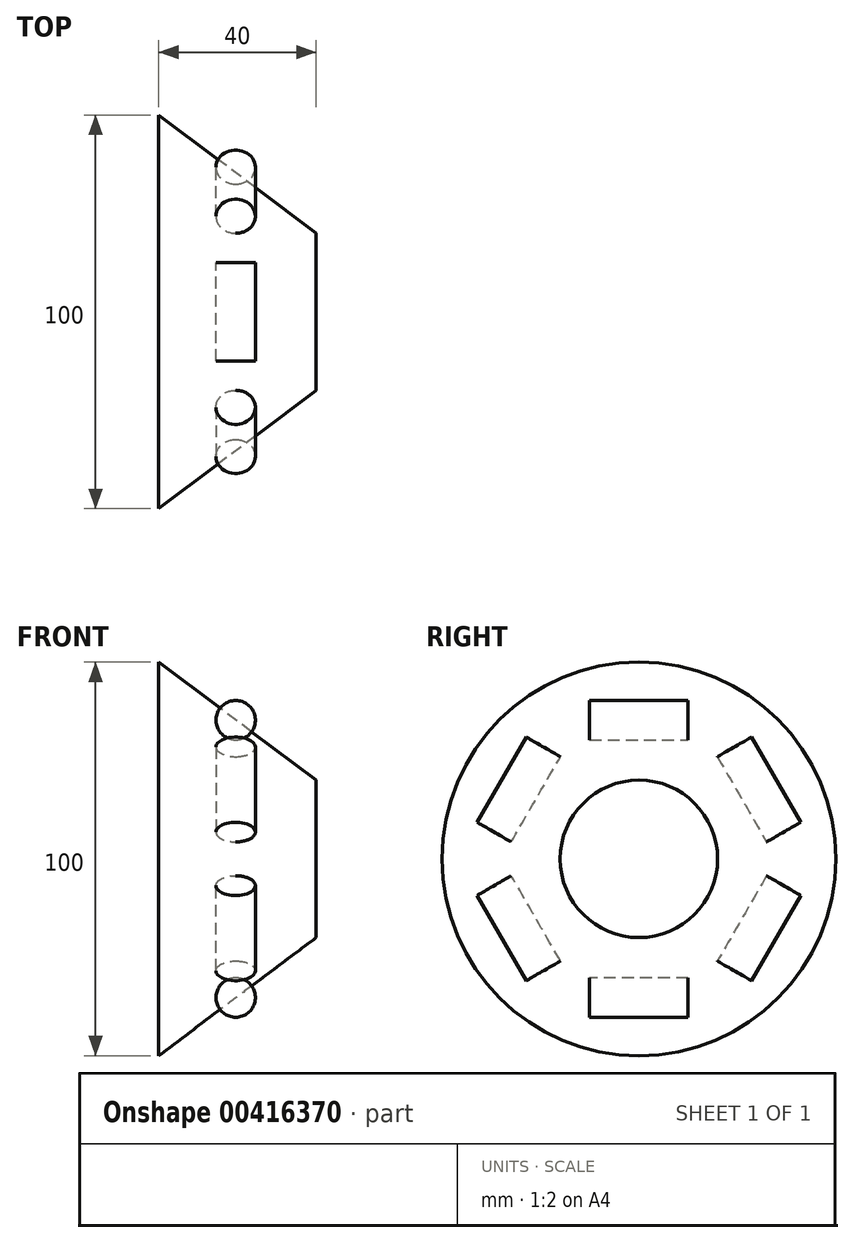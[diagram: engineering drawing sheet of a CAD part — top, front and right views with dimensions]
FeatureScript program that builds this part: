
annotation { "Feature Type Name" : "Feature", "Feature Type Description" : "" }
export const myFeature = defineFeature(function(context is Context, id is Id, definition is map)
    precondition{}
    {
        {
            var Q0;
            Q0=qCreatedBy(makeId("Right.planeOp"),FACE);
            var sketch = newSketch(context, id + "F0", { "sketchPlane" : qUnion([Q0])});
            skCircle(sketch, "E0", {"center": v(0, 0) * mm, "radius": 50 * mm});
            skSolve(sketch);
        }
        {
            var Q0;
            Q0=qCreatedBy(makeId("Right.planeOp"),FACE);
            cPlane(context, id + "F1", {"entities" : qUnion([Q0]), "cplaneType" : CPlaneType.OFFSET, "offset" : 40 * mm, "width" : 150 * mm, "height" : 150 * mm});
        }
        {
            var Q0;
            Q0=qCreatedBy(id+"F1.planeOp",FACE);
            var sketch = newSketch(context, id + "F2", { "sketchPlane" : qUnion([Q0])});
            skCircle(sketch, "E1", {"center": v(0, 0) * mm, "radius": 20 * mm});
            skSolve(sketch);
        }
        {
            var Q0;
            Q0=makeQuery(id+"F0.imprint","IMPRINT",FACE,{"disambiguationData":[TD([[makeQuery(id+"F0.imprint","IMPRINT",EDGE,{"derivedFrom":sQuery(id+"F0.wireOp",EDGE,"E0")}),1.0]])]});
            var Q1;
            Q1=makeQuery(id+"F2.imprint","IMPRINT",FACE,{"disambiguationData":[TD([[makeQuery(id+"F2.imprint","IMPRINT",EDGE,{"derivedFrom":sQuery(id+"F2.wireOp",EDGE,"E1")}),1.0]])]});
            loft(context, id + "F3", {"sheetProfilesArray" : [{ "sheetProfileEntities" : qUnion([Q0]) }, { "sheetProfileEntities" : qUnion([Q1]) }]});
        }
        {
            var Q0;
            Q0=qCreatedBy(makeId("Front.planeOp"),FACE);
            var sketch = newSketch(context, id + "F4", { "sketchPlane" : qUnion([Q0])});
            skCircle(sketch, "E2", {"center": v(19.57, 35.24) * mm, "radius": 5 * mm});
            skLineSegment(sketch, "E3", {"start": v(0, 0) * mm, "end": v(-15, 0) * mm});
            skSolve(sketch);
        }
        {
            var Q0;
            Q0=makeQuery(id+"F4.imprint","IMPRINT",FACE,{"disambiguationData":[TD([[makeQuery(id+"F4.imprint","IMPRINT",EDGE,{"derivedFrom":sQuery(id+"F4.wireOp",EDGE,"E2")}),1.0]])]});
            extrude(context, id + "F5", {"entities" : qUnion([Q0]), "endBound" : BoundingType.SYMMETRIC, "depth" : 25 * mm});
        }
        {
            var Q0;
            Q0=makeQuery(id+"F5.opExtrude","SWEPT_BODY",BODY,{"disambiguationData":[OSD([sQuery(id+"F4.wireOp",EDGE,"E2")])]});
            var Q1;
            Q1=sQuery(id+"F4.wireOp",EDGE,"E3");
            circularPattern(context, id + "F6", {"entities" : qUnion([Q0]), "axis" : qUnion([Q1]), "angle" : 360 * degree, "instanceCount" : 6, "equalSpace" : true});
        }
    });
